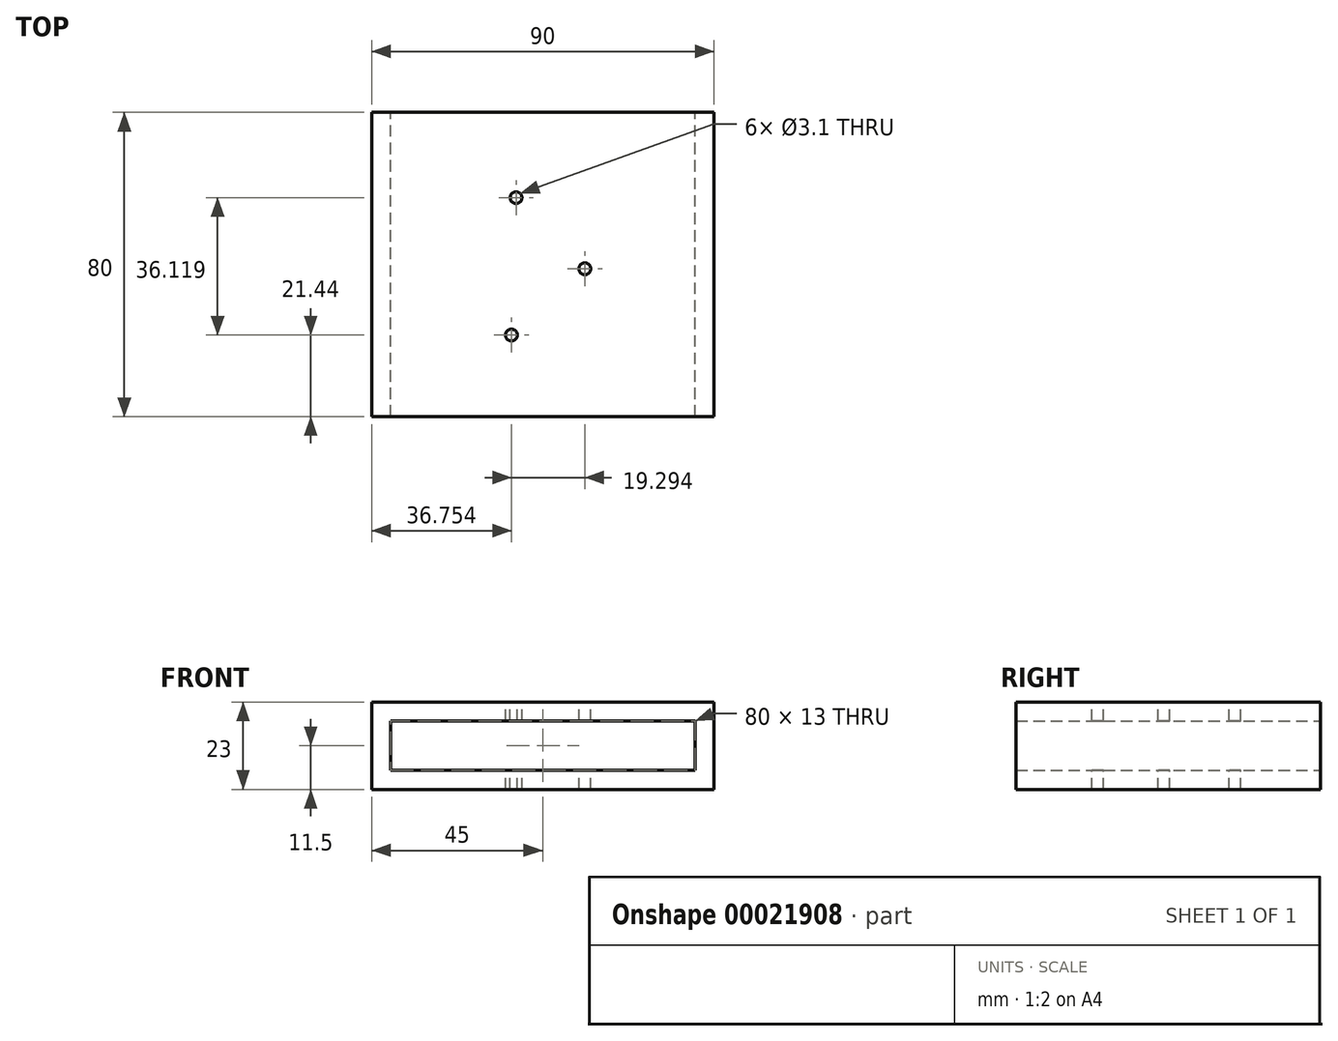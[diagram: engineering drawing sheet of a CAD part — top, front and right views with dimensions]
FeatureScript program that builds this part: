
annotation { "Feature Type Name" : "Feature", "Feature Type Description" : "" }
export const myFeature = defineFeature(function(context is Context, id is Id, definition is map)
    precondition{}
    {
        {
            var Q0;
            Q0=qCreatedBy(makeId("Front.planeOp"),FACE);
            var sketch = newSketch(context, id + "F0", { "sketchPlane" : qUnion([Q0])});
            skLineSegment(sketch, "E0.bottom", {"start": v(0, 0) * mm, "end": v(90, 0) * mm});
            skLineSegment(sketch, "E0.top", {"start": v(0, 23) * mm, "end": v(90, 23) * mm});
            skLineSegment(sketch, "E0.left", {"start": v(0, 0) * mm, "end": v(0, 23) * mm});
            skLineSegment(sketch, "E0.right", {"start": v(90, 0) * mm, "end": v(90, 23) * mm});
            skLineSegment(sketch, "E1.bottom", {"start": v(5, 5) * mm, "end": v(85, 5) * mm});
            skLineSegment(sketch, "E1.top", {"start": v(5, 18) * mm, "end": v(85, 18) * mm});
            skLineSegment(sketch, "E1.left", {"start": v(5, 5) * mm, "end": v(5, 18) * mm});
            skLineSegment(sketch, "E1.right", {"start": v(85, 5) * mm, "end": v(85, 18) * mm});
            skSolve(sketch);
        }
        {
            var Q0;
            Q0=makeQuery(id+"F0.imprint","IMPRINT",FACE,{"disambiguationData":[TD([[makeQuery(id+"F0.imprint","IMPRINT",EDGE,{"derivedFrom":sQuery(id+"F0.wireOp",EDGE,"E0.bottom")}),1.0]])]});
            extrude(context, id + "F1", {"entities" : qUnion([Q0]), "depth" : 80 * mm});
        }
        {
            var Q0;
            Q0=makeQuery(id+"F1.opExtrude","SWEPT_FACE",FACE,{"disambiguationData":[OSD([sQuery(id+"F0.wireOp",EDGE,"E0.top")])]});
            var sketch = newSketch(context, id + "F2", { "sketchPlane" : qUnion([Q0])});
            skCircle(sketch, "E2", {"center": v(37.97, -22.44) * mm, "radius": 1.55 * mm});
            skCircle(sketch, "E3", {"center": v(56.05, -41.13) * mm, "radius": 1.55 * mm});
            skCircle(sketch, "E4", {"center": v(36.75, -58.56) * mm, "radius": 1.55 * mm});
            skSolve(sketch);
        }
        {
            var Q0;
            Q0=makeQuery(id+"F2.imprint","IMPRINT",FACE,{"disambiguationData":[TD([[makeQuery(id+"F2.imprint","IMPRINT",EDGE,{"derivedFrom":sQuery(id+"F2.wireOp",EDGE,"E2")}),1.0]])]});
            var Q1;
            Q1=makeQuery(id+"F2.imprint","IMPRINT",FACE,{"disambiguationData":[TD([[makeQuery(id+"F2.imprint","IMPRINT",EDGE,{"derivedFrom":sQuery(id+"F2.wireOp",EDGE,"E3")}),1.0]])]});
            var Q2;
            Q2=makeQuery(id+"F2.imprint","IMPRINT",FACE,{"disambiguationData":[TD([[makeQuery(id+"F2.imprint","IMPRINT",EDGE,{"derivedFrom":sQuery(id+"F2.wireOp",EDGE,"E4")}),1.0]])]});
            extrude(context, id + "F3", {"entities" : qUnion([Q0, Q1, Q2]), "operationType" : NewBodyOperationType.REMOVE, "endBound" : BoundingType.THROUGH_ALL, "oppositeDirection" : true, "depth" : 25 * mm});
        }
    });
